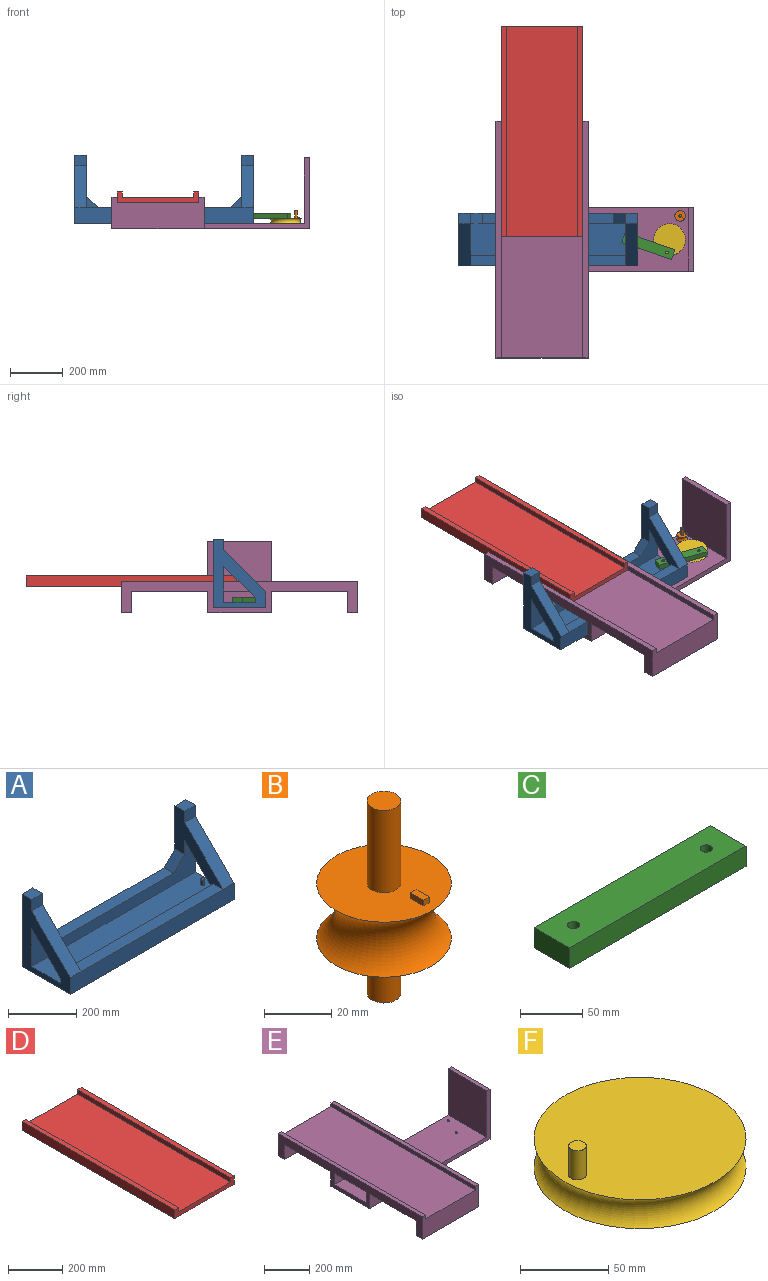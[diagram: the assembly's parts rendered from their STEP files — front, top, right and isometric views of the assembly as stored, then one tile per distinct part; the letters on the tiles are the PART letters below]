
ASSEMBLY  parts=6 mates=6
PART A: 24 faces, bbox 680x200x260 mm
  f0: plane 223.64x200mm, normal (1,0,0), area 14636.8mm2, adj f3,f4,f5,f6,f8,f14,f18,f19
  f1: plane 500x40mm, normal (0,0,1), area 20000mm2, adj f6,f8,f20,f21
  f2: plane 223.64x200mm, normal (-1,0,0), area 14636.8mm2, adj f3,f5,f6,f8,f13,f15,f16,f17
  f3: plane 590x40mm, normal (0,0,1), area 23600mm2, adj f0,f2,f5,f9
  f4: plane 45x40mm, normal (0,-1,0), area 1800mm2, adj f0,f12,f14,f18
  f5: plane 680x40mm, normal (0,1,0), area 25072.4mm2, adj f0,f2,f3,f7,f11,f12,f17,f19
  f6: plane 680x136.36mm, normal (0,-1,0), area 37897.4mm2, adj f0,f1,f2,f7,f11,f12,f17,f19
  f7: plane 680x120mm, normal (0,0,1), area 81521.5mm2, adj f5,f6,f11,f12,f22
  f8: plane 680x260mm, normal (0,1,0), area 60825mm2, adj f0,f1,f2,f10,f11,f12,f14,f15
  f9: plane 680x60mm, normal (0,-1,0), area 40800mm2, adj f3,f10,f11,f12,f16,f18
  f10: plane 680x200mm, normal (0,0,-1), area 136000mm2, adj f8,f9,f11,f12
  f11: plane 260x200mm, normal (1,0,0), area 23636.8mm2, adj f5,f6,f7,f8,f9,f10,f13,f15
  f12: plane 260x200mm, normal (-1,0,0), area 23636.8mm2, adj f4,f5,f6,f7,f8,f9,f10,f14
  f13: plane 45x40mm, normal (0,-1,0), area 1800mm2, adj f2,f11,f15,f16
  f14: plane 45x40mm, normal (0,0,1), area 1800mm2, adj f0,f4,f8,f12
  f15: plane 45x40mm, normal (0,0,1), area 1800mm2, adj f2,f8,f11,f13
  f16: plane 160x160mm, normal (0,-0.71,0.71), area 10182.3mm2, adj f2,f9,f11,f13
  f17: plane 120x120mm, normal (0,0.71,-0.71), area 7636.8mm2, adj f2,f5,f6,f11
  f18: plane 160x160mm, normal (0,-0.71,0.71), area 10182.3mm2, adj f0,f4,f9,f12
  f19: plane 120x120mm, normal (0,0.71,-0.71), area 7636.8mm2, adj f0,f5,f6,f12
  f20: plane 45x45mm, normal (-0.71,0,0.71), area 2545.6mm2, adj f1,f2,f6,f8
  f21: plane 45x45mm, normal (0.71,0,0.71), area 2545.6mm2, adj f0,f1,f6,f8
  f22: cone r=5mm half-angle=3deg, axis (0,0,1), area 695.1mm2, adj f7,f23
  f23: plane 12.1x12.1mm, normal (0,0,1), area 114.9mm2, adj f22
PART B: 12 faces, bbox 57.8x57.8x70 mm
  f0: plane 40x40mm, normal (0,0,1), area 1164.2mm2, adj f1,f6,f7,f8,f9,f10
  f1: cylinder r=5mm len=30mm, axis (0,0,-1), area 942.5mm2, adj f0,f2
  f2: plane 10x10mm, normal (0,0,1), area 78.5mm2, adj f1
  f3: plane 10x10mm, normal (0,0,-1), area 78.5mm2, adj f4
  f4: cylinder r=5mm len=20mm, axis (0,0,-1), area 628.3mm2, adj f3,f5
  f5: plane 40x40mm, normal (0,0,-1), area 1178.1mm2, adj f4,f6
  f6: torus R=26.7mm, axis (0,0,-1), area 2447.3mm2, adj f0,f5
  f7: plane 2.5x2mm, normal (0,1,0), area 5mm2, adj f0,f8,f10,f11
  f8: plane 5.54x2mm, normal (-1,0,0), area 11.1mm2, adj f0,f7,f9,f11
  f9: plane 2.5x2mm, normal (0,-1,0), area 5mm2, adj f0,f8,f10,f11
  f10: plane 5.54x2mm, normal (1,0,0), area 11.1mm2, adj f0,f7,f9,f11
  f11: plane 5.54x2.5mm, normal (0,0,1), area 13.9mm2, adj f7,f8,f9,f10
PART C: 8 faces, bbox 200x40x20 mm
  f0: plane 40x20mm, normal (1,0,0), area 800mm2, adj f1,f3,f4,f5
  f1: plane 200x20mm, normal (0,1,0), area 4000mm2, adj f0,f2,f4,f5
  f2: plane 40x20mm, normal (-1,0,0), area 800mm2, adj f1,f3,f4,f5
  f3: plane 200x20mm, normal (0,-1,0), area 4000mm2, adj f0,f2,f4,f5
  f4: plane 200x40mm, normal (0,0,1), area 7842.9mm2, adj f0,f1,f2,f3,f6,f7
  f5: plane 200x40mm, normal (0,0,-1), area 7842.9mm2, adj f0,f1,f2,f3,f6,f7
  f6: cylinder r=5mm len=20mm, axis (0,0,1), area 628.3mm2, adj f4,f5
  f7: cylinder r=5mm len=20mm, axis (0,0,1), area 628.3mm2, adj f4,f5
PART D: 10 faces, bbox 310x800x40 mm
  f0: plane 800x40mm, normal (1,0,0), area 32000mm2, adj f1,f3,f5,f9
  f1: plane 310x40mm, normal (0,1,0), area 7000mm2, adj f0,f2,f4,f5,f6,f7,f8,f9
  f2: plane 800x40mm, normal (-1,0,0), area 32000mm2, adj f1,f3,f5,f7
  f3: plane 310x40mm, normal (0,-1,0), area 7000mm2, adj f0,f2,f4,f5,f6,f7,f8,f9
  f4: plane 800x270mm, normal (0,0,1), area 216000mm2, adj f1,f3,f6,f8
  f5: plane 800x310mm, normal (0,0,-1), area 248000mm2, adj f0,f1,f2,f3
  f6: plane 800x20mm, normal (1,0,0), area 16000mm2, adj f1,f3,f4,f7
  f7: plane 800x20mm, normal (0,0,1), area 16000mm2, adj f1,f2,f3,f6
  f8: plane 800x20mm, normal (-1,0,0), area 16000mm2, adj f1,f3,f4,f9
  f9: plane 800x20mm, normal (0,0,1), area 16000mm2, adj f0,f1,f3,f8
PART E: 27 faces, bbox 750x900x270 mm
  f0: plane 900x120mm, normal (1,0,0), area 44800mm2, adj f2,f3,f4,f5,f7,f8,f10,f11
  f1: plane 900x310mm, normal (0,0,1), area 279000mm2, adj f5,f7,f18,f20
  f2: plane 350x290mm, normal (0,0,-1), area 101500mm2, adj f0,f6,f12,f16
  f3: plane 350x200mm, normal (0,0,-1), area 70000mm2, adj f0,f6,f11,f13
  f4: plane 350x290mm, normal (0,0,-1), area 101500mm2, adj f0,f6,f8,f14
  f5: plane 350x120mm, normal (0,1,0), area 35800mm2, adj f0,f1,f6,f17,f18,f19,f20,f21
  f6: plane 900x120mm, normal (-1,0,0), area 49600mm2, adj f2,f3,f4,f5,f7,f8,f9,f10
  f7: plane 350x120mm, normal (0,-1,0), area 35800mm2, adj f0,f1,f6,f15,f18,f19,f20,f21
  f8: plane 750x270mm, normal (0,-1,0), area 41000mm2, adj f0,f4,f6,f9,f10,f22,f23,f24
  f9: plane 750x240mm, normal (0,0,-1), area 179842.9mm2, adj f6,f8,f12,f22,f25,f26
  f10: plane 730x240mm, normal (0,0,1), area 161042.9mm2, adj f0,f6,f8,f11,f12,f13,f23,f25
  f11: plane 350x60mm, normal (0,1,0), area 21000mm2, adj f0,f3,f6,f10
  f12: plane 750x270mm, normal (0,1,0), area 41000mm2, adj f0,f2,f6,f9,f10,f22,f23,f24
  f13: plane 350x60mm, normal (0,-1,0), area 21000mm2, adj f0,f3,f6,f10
  f14: plane 350x80mm, normal (0,1,0), area 28000mm2, adj f0,f4,f6,f15
  f15: plane 350x40mm, normal (0,0,-1), area 14000mm2, adj f0,f6,f7,f14
  f16: plane 350x80mm, normal (0,-1,0), area 28000mm2, adj f0,f2,f6,f17
  f17: plane 350x40mm, normal (0,0,-1), area 14000mm2, adj f0,f5,f6,f16
  f18: plane 900x20mm, normal (1,0,0), area 18000mm2, adj f1,f5,f7,f19
  f19: plane 900x20mm, normal (0,0,1), area 18000mm2, adj f5,f6,f7,f18
  f20: plane 900x20mm, normal (-1,0,0), area 18000mm2, adj f1,f5,f7,f21
  f21: plane 900x20mm, normal (0,0,1), area 18000mm2, adj f0,f5,f7,f20
  f22: plane 270x240mm, normal (1,0,0), area 64800mm2, adj f8,f9,f12,f24
  f23: plane 250x240mm, normal (-1,0,0), area 60000mm2, adj f8,f10,f12,f24
  f24: plane 240x20mm, normal (0,0,1), area 4800mm2, adj f8,f12,f22,f23
  f25: cylinder r=5mm len=20mm, axis (0,0,1), area 628.3mm2, adj f9,f10
  f26: cylinder r=5mm len=20mm, axis (0,0,1), area 628.3mm2, adj f9,f10
PART F: 7 faces, bbox 144.4x144.4x60 mm
  f0: plane 120x120mm, normal (0,0,1), area 11231.2mm2, adj f4,f5
  f1: plane 10x10mm, normal (0,0,-1), area 78.5mm2, adj f2
  f2: cylinder r=5mm len=20mm, axis (0,0,-1), area 628.3mm2, adj f1,f3
  f3: plane 120x120mm, normal (0,0,-1), area 11231.2mm2, adj f2,f4
  f4: torus R=66.7mm, axis (0,0,-1), area 8379.7mm2, adj f0,f3
  f5: cylinder r=5mm len=20mm, axis (0,0,-1), area 628.3mm2, adj f0,f6
  f6: plane 10x10mm, normal (0,0,1), area 78.5mm2, adj f5
PLACE A t=(-417.32,0,-50)mm
PLACE B rot(axis=(0,0,1),45.4deg) t=(84.29,90,-80)mm
PLACE C rot(axis=(0,0,-1),19.1deg) t=(-36.44,-24.51,-40)mm
PLACE D t=(-440.71,411.35,20)mm
PLACE E t=(-440.71,0,0)mm fixed
PLACE F rot(axis=(0,0,1),78.6deg) t=(44.29,0,-80)mm
MATE revolute C.f7 <-> F.f5  axis (0,0,1) through (34.44,-49.02,-20)mm
MATE slider A.f11 <-> E.f0  axis (1,0,0) through (-77.32,-100,0)mm
MATE revolute B.f1 <-> E.f26  axis (0,0,-1) through (84.29,90,-80)mm
MATE revolute C.f6 <-> A.f22  axis (0,0,1) through (-107.32,0,-20)mm
MATE revolute F.f2 <-> E.f25  axis (0,0,-1) through (44.29,0,-80)mm
MATE slider E.f5 <-> D.f1  axis (0,1,0) through (-595.71,450,20)mm
